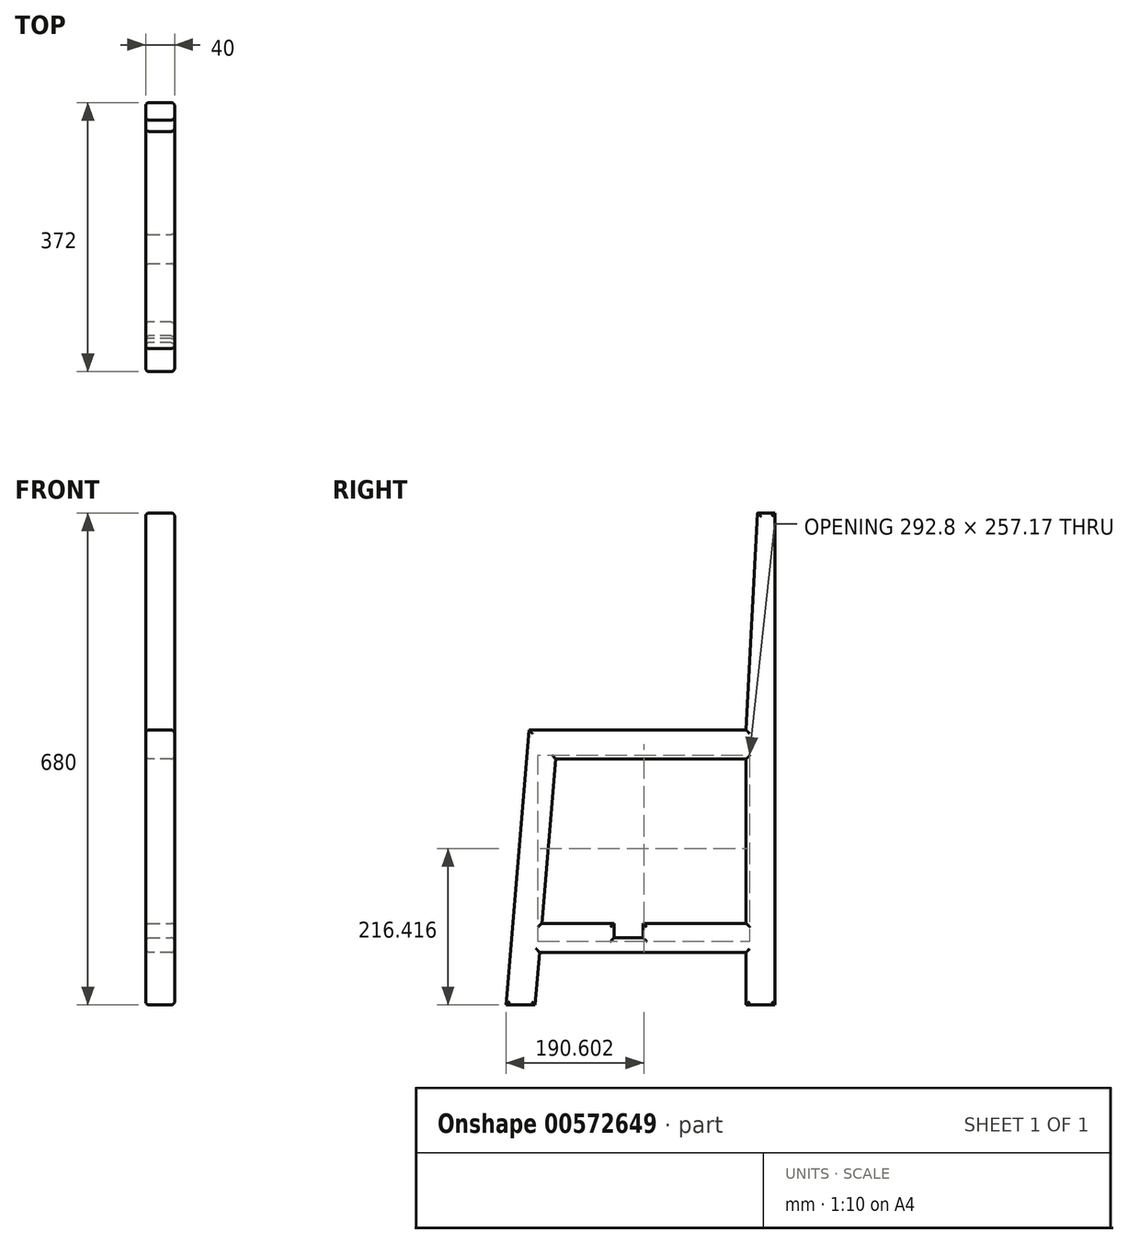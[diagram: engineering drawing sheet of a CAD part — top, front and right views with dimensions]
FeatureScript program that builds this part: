
annotation { "Feature Type Name" : "Feature", "Feature Type Description" : "" }
export const myFeature = defineFeature(function(context is Context, id is Id, definition is map)
    precondition{}
    {
        {
            var Q0;
            Q0=qCreatedBy(makeId("Right.planeOp"),FACE);
            var sketch = newSketch(context, id + "F0", { "sketchPlane" : qUnion([Q0])});
            skLineSegment(sketch, "E0", {"start": v(-184, 0) * mm, "end": v(-152, 380) * mm});
            skLineSegment(sketch, "E1", {"start": v(-152, 380) * mm, "end": v(148, 380) * mm});
            skLineSegment(sketch, "E2", {"start": v(148, 380) * mm, "end": v(163.72, 680) * mm});
            skLineSegment(sketch, "E3", {"start": v(163.72, 680) * mm, "end": v(188, 680) * mm});
            skLineSegment(sketch, "E4", {"start": v(188, 680) * mm, "end": v(188, 0) * mm});
            skLineSegment(sketch, "E5", {"start": v(188, 0) * mm, "end": v(148, 0) * mm});
            skLineSegment(sketch, "E6", {"start": v(148, 0) * mm, "end": v(148, 72.83) * mm});
            skLineSegment(sketch, "E7", {"start": v(148, 72.83) * mm, "end": v(-137.73, 72.83) * mm});
            skLineSegment(sketch, "E8", {"start": v(-137.73, 72.83) * mm, "end": v(-143.86, 0) * mm});
            skLineSegment(sketch, "E9", {"start": v(-143.86, 0) * mm, "end": v(-184, 0) * mm});
            skLineSegment(sketch, "E10", {"start": v(-134.36, 112.83) * mm, "end": v(-115.23, 340) * mm});
            skLineSegment(sketch, "E11", {"start": v(-115.23, 340) * mm, "end": v(148, 340) * mm});
            skLineSegment(sketch, "E12", {"start": v(148, 340) * mm, "end": v(148, 112.83) * mm});
            skLineSegment(sketch, "E13", {"start": v(148, 112.83) * mm, "end": v(-134.36, 112.83) * mm});
            skSolve(sketch);
        }
        {
            var Q0;
            Q0 = qSketchRegion(id + "F0", true);
            extrude(context, id + "F1", {"entities" : qUnion([Q0]), "depth" : 40 * mm, "offsetDistance" : 25 * mm});
        }
        {
            var Q0;
            Q0=makeQuery(id+"F1.opExtrude","CAP_FACE",FACE,{"disambiguationData":[OSD([sQuery(id+"F0.wireOp",EDGE,"E0"),sQuery(id+"F0.wireOp",EDGE,"E1"),sQuery(id+"F0.wireOp",EDGE,"E2"),sQuery(id+"F0.wireOp",EDGE,"E3"),sQuery(id+"F0.wireOp",EDGE,"E4"),sQuery(id+"F0.wireOp",EDGE,"E5"),sQuery(id+"F0.wireOp",EDGE,"E6"),sQuery(id+"F0.wireOp",EDGE,"E7"),sQuery(id+"F0.wireOp",EDGE,"E8"),sQuery(id+"F0.wireOp",EDGE,"E9"),sQuery(id+"F0.wireOp",EDGE,"E10"),sQuery(id+"F0.wireOp",EDGE,"E11"),sQuery(id+"F0.wireOp",EDGE,"E12"),sQuery(id+"F0.wireOp",EDGE,"E13")])],"isStart":false});
            var sketch = newSketch(context, id + "F2", { "sketchPlane" : qUnion([Q0])});
            skLineSegment(sketch, "E14.bottom", {"start": v(-34.65, 112.83) * mm, "end": v(5.35, 112.83) * mm});
            skLineSegment(sketch, "E14.top", {"start": v(-34.65, 92.83) * mm, "end": v(5.35, 92.83) * mm});
            skLineSegment(sketch, "E14.left", {"start": v(-34.65, 112.83) * mm, "end": v(-34.65, 92.83) * mm});
            skLineSegment(sketch, "E14.right", {"start": v(5.35, 112.83) * mm, "end": v(5.35, 92.83) * mm});
            skSolve(sketch);
        }
        {
            var Q0;
            Q0 = qSketchRegion(id + "F2", true);
            extrude(context, id + "F3", {"entities" : qUnion([Q0]), "operationType" : NewBodyOperationType.REMOVE, "endBound" : BoundingType.THROUGH_ALL, "oppositeDirection" : true, "depth" : 25 * mm, "offsetDistance" : 25 * mm});
        }
        {
            var Q0;
            Q0=makeQuery(id+"F1.opExtrude","CAP_FACE",FACE,{"disambiguationData":[OSD([sQuery(id+"F0.wireOp",EDGE,"E0"),sQuery(id+"F0.wireOp",EDGE,"E1"),sQuery(id+"F0.wireOp",EDGE,"E2"),sQuery(id+"F0.wireOp",EDGE,"E3"),sQuery(id+"F0.wireOp",EDGE,"E4"),sQuery(id+"F0.wireOp",EDGE,"E5"),sQuery(id+"F0.wireOp",EDGE,"E6"),sQuery(id+"F0.wireOp",EDGE,"E7"),sQuery(id+"F0.wireOp",EDGE,"E8"),sQuery(id+"F0.wireOp",EDGE,"E9"),sQuery(id+"F0.wireOp",EDGE,"E10"),sQuery(id+"F0.wireOp",EDGE,"E11"),sQuery(id+"F0.wireOp",EDGE,"E12"),sQuery(id+"F0.wireOp",EDGE,"E13")])],"isStart":false});
            var Q1;
            Q1=makeQuery(id+"F1.opExtrude","CAP_FACE",FACE,{"disambiguationData":[OSD([sQuery(id+"F0.wireOp",EDGE,"E0"),sQuery(id+"F0.wireOp",EDGE,"E1"),sQuery(id+"F0.wireOp",EDGE,"E2"),sQuery(id+"F0.wireOp",EDGE,"E3"),sQuery(id+"F0.wireOp",EDGE,"E4"),sQuery(id+"F0.wireOp",EDGE,"E5"),sQuery(id+"F0.wireOp",EDGE,"E6"),sQuery(id+"F0.wireOp",EDGE,"E7"),sQuery(id+"F0.wireOp",EDGE,"E8"),sQuery(id+"F0.wireOp",EDGE,"E9"),sQuery(id+"F0.wireOp",EDGE,"E10"),sQuery(id+"F0.wireOp",EDGE,"E11"),sQuery(id+"F0.wireOp",EDGE,"E12"),sQuery(id+"F0.wireOp",EDGE,"E13")])],"isStart":true});
            fillet(context, id + "F4", {"entities" : qUnion([Q0, Q1]), "radius" : 5 * mm, "tangentPropagation" : true, "allowEdgeOverflow" : false});
        }
    });
